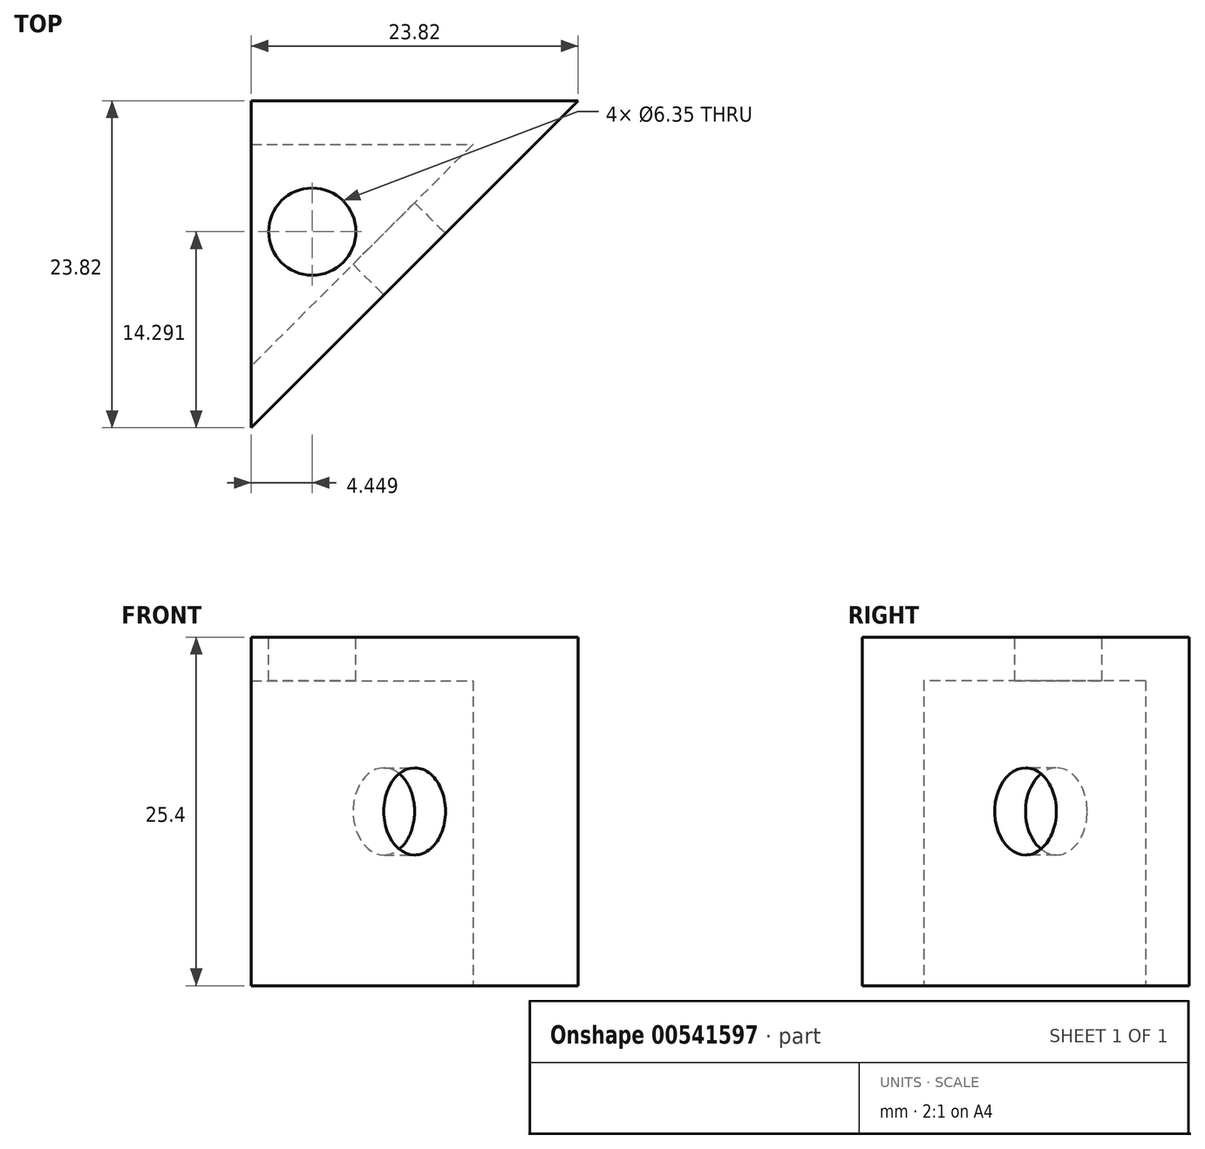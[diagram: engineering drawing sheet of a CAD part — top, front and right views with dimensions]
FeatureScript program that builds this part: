
annotation { "Feature Type Name" : "Feature", "Feature Type Description" : "" }
export const myFeature = defineFeature(function(context is Context, id is Id, definition is map)
    precondition{}
    {
        {
            var Q0;
            Q0=qCreatedBy(makeId("Top.planeOp"),FACE);
            var sketch = newSketch(context, id + "F0", { "sketchPlane" : qUnion([Q0])});
            skLineSegment(sketch, "E0.bottom", {"start": v(-11.9, 11.9) * mm, "end": v(11.9, 11.9) * mm});
            skLineSegment(sketch, "E0.top", {"start": v(-11.9, -11.9) * mm, "end": v(11.9, -11.9) * mm});
            skLineSegment(sketch, "E0.left", {"start": v(-11.9, 11.9) * mm, "end": v(-11.9, -11.9) * mm});
            skLineSegment(sketch, "E0.right", {"start": v(11.9, 11.9) * mm, "end": v(11.9, -11.9) * mm});
            skPoint(sketch, "E0.middle", {"position": v(0, 0) * mm});
            skLineSegment(sketch, "E1", {"start": v(11.9, 11.9) * mm, "end": v(-11.9, -11.9) * mm});
            skSolve(sketch);
        }
        {
            var Q0;
            Q0=makeQuery(id+"F0.imprint","IMPRINT",FACE,{"disambiguationData":[TD([[makeQuery(id+"F0.imprint","IMPRINT",EDGE,{"derivedFrom":sQuery(id+"F0.wireOp",EDGE,"E0.bottom")}),-1.0]])]});
            extrude(context, id + "F1", {"entities" : qUnion([Q0]), "depth" : 25.4 * mm, "offsetDistance" : 25.4 * mm});
        }
        {
            var Q0;
            Q0=makeQuery(id+"F1.opExtrude","SWEPT_FACE",FACE,{"disambiguationData":[OSD([sQuery(id+"F0.wireOp",EDGE,"E0.left")])]});
            shell(context, id + "F2", {"entities" : qUnion([Q0]), "thickness" : 3.17 * mm});
        }
        {
            var Q0;
            {var subQ0=sQuery(id+"F0.wireOp",EDGE,"E1");var subQ1=sQuery(id+"F0.wireOp",EDGE,"E0.left");var subQ2=sQuery(id+"F0.wireOp",EDGE,"E0.bottom");Q0=makeQuery(id+"F2.opShell","OFFSET_FACE",FACE,{"disambiguationData":[OSD([subQ2,subQ1,subQ0]),TDD([makeQuery(id+"F1.opExtrude","CAP_FACE",FACE,{"disambiguationData":[OSD([subQ2,subQ1,subQ0])],"isStart":true})])]});}
            extrude(context, id + "F3", {"entities" : qUnion([Q0]), "operationType" : NewBodyOperationType.REMOVE, "oppositeDirection" : true, "depth" : 25.4 * mm, "offsetDistance" : 25.4 * mm});
        }
        {
            var Q0;
            Q0=makeQuery(id+"F1.opExtrude","SWEPT_FACE",FACE,{"disambiguationData":[OSD([sQuery(id+"F0.wireOp",EDGE,"E0.left")])]});
            var sketch = newSketch(context, id + "F4", { "sketchPlane" : qUnion([Q0])});
            skLineSegment(sketch, "E2", {"start": v(11.9, 25.4) * mm, "end": v(-11.9, 0) * mm});
            skLineSegment(sketch, "E3", {"start": v(-11.9, 25.4) * mm, "end": v(11.9, 0) * mm});
            skCircle(sketch, "E4", {"center": v(0, 12.7) * mm, "radius": 3.18 * mm});
            skSolve(sketch);
        }
        {
            var Q0;
            {var subQ0=sQuery(id+"F4.wireOp",EDGE,"E4");var subQ1=sQuery(id+"F4.wireOp",EDGE,"E2");var subQ2=makeQuery(id+"F4.imprint","INTERSECT",VERTEX,{"disambiguationData":[OD(0.0)],"derivedFrom":[subQ1,subQ0]});Q0=makeQuery(id+"F4.imprint","IMPRINT",FACE,{"disambiguationData":[TD([[makeQuery(id+"F4.imprint","IMPRINT",EDGE,{"disambiguationData":[TD([[subQ2,-1.0]])],"derivedFrom":subQ1}),1.0]])]});}
            var Q1;
            {var subQ0=sQuery(id+"F4.wireOp",EDGE,"E4");var subQ1=sQuery(id+"F4.wireOp",EDGE,"E2");var subQ2=makeQuery(id+"F4.imprint","INTERSECT",VERTEX,{"disambiguationData":[OD(0.0)],"derivedFrom":[subQ1,subQ0]});Q1=makeQuery(id+"F4.imprint","IMPRINT",FACE,{"disambiguationData":[TD([[makeQuery(id+"F4.imprint","IMPRINT",EDGE,{"disambiguationData":[TD([[subQ2,-1.0]])],"derivedFrom":subQ1}),-1.0]])]});}
            var Q2;
            {var subQ0=sQuery(id+"F4.wireOp",EDGE,"E3");var subQ1=sQuery(id+"F4.wireOp",EDGE,"E2");var subQ2=makeQuery(id+"F4.imprint","INTERSECT",VERTEX,{"derivedFrom":[subQ1,subQ0]});Q2=makeQuery(id+"F4.imprint","IMPRINT",FACE,{"disambiguationData":[TD([[makeQuery(id+"F4.imprint","IMPRINT",EDGE,{"disambiguationData":[TD([[subQ2,-1.0]])],"derivedFrom":subQ1}),-1.0]])]});}
            var Q3;
            {var subQ0=sQuery(id+"F4.wireOp",EDGE,"E3");var subQ1=sQuery(id+"F4.wireOp",EDGE,"E2");var subQ2=makeQuery(id+"F4.imprint","INTERSECT",VERTEX,{"derivedFrom":[subQ1,subQ0]});Q3=makeQuery(id+"F4.imprint","IMPRINT",FACE,{"disambiguationData":[TD([[makeQuery(id+"F4.imprint","IMPRINT",EDGE,{"disambiguationData":[TD([[subQ2,-1.0]])],"derivedFrom":subQ1}),1.0]])]});}
            extrude(context, id + "F5", {"entities" : qUnion([Q0, Q1, Q2, Q3]), "operationType" : NewBodyOperationType.REMOVE, "oppositeDirection" : true, "depth" : 3.17 * mm, "offsetDistance" : 25.4 * mm});
        }
        {
            var Q0;
            Q0=makeQuery(id+"F1.opExtrude","CAP_FACE",FACE,{"disambiguationData":[OSD([sQuery(id+"F0.wireOp",EDGE,"E0.bottom"),sQuery(id+"F0.wireOp",EDGE,"E0.left"),sQuery(id+"F0.wireOp",EDGE,"E1")])],"isStart":false});
            var sketch = newSketch(context, id + "F6", { "sketchPlane" : qUnion([Q0])});
            skCircle(sketch, "E5", {"center": v(-7.46, 2.38) * mm, "radius": 3.18 * mm});
            skSolve(sketch);
        }
        {
            var Q0;
            {var subQ0=sQuery(id+"F6.wireOp",EDGE,"E5");var subQ1=sQuery(id+"F6.wireOp",EDGE,"HWwZXyzN-BkNU-UMwY-gXSM-99bSMozpZ1Sp");var subQ2=makeQuery(id+"F6.imprint","INTERSECT",VERTEX,{"disambiguationData":[OD(0.0)],"derivedFrom":[subQ1,subQ0]});Q0=makeQuery(id+"F6.imprint","IMPRINT",FACE,{"disambiguationData":[TD([[makeQuery(id+"F6.imprint","IMPRINT",EDGE,{"disambiguationData":[TD([[subQ2,-1.0]])],"derivedFrom":subQ1}),-1.0]])]});}
            var Q1;
            {var subQ0=sQuery(id+"F6.wireOp",EDGE,"E5");var subQ1=sQuery(id+"F6.wireOp",EDGE,"HWwZXyzN-BkNU-UMwY-gXSM-99bSMozpZ1Sp");var subQ2=makeQuery(id+"F6.imprint","INTERSECT",VERTEX,{"disambiguationData":[OD(0.0)],"derivedFrom":[subQ1,subQ0]});Q1=makeQuery(id+"F6.imprint","IMPRINT",FACE,{"disambiguationData":[TD([[makeQuery(id+"F6.imprint","IMPRINT",EDGE,{"disambiguationData":[TD([[subQ2,-1.0]])],"derivedFrom":subQ1}),1.0]])]});}
            var Q2;
            {var subQ0=sQuery(id+"F6.wireOp",EDGE,"xwTGamvL-BoM2-GFio-XRPn-19hndFO4djhj");var subQ1=sQuery(id+"F6.wireOp",EDGE,"HWwZXyzN-BkNU-UMwY-gXSM-99bSMozpZ1Sp");var subQ2=makeQuery(id+"F6.imprint","INTERSECT",VERTEX,{"derivedFrom":[subQ1,subQ0]});Q2=makeQuery(id+"F6.imprint","IMPRINT",FACE,{"disambiguationData":[TD([[makeQuery(id+"F6.imprint","IMPRINT",EDGE,{"disambiguationData":[TD([[subQ2,-1.0]])],"derivedFrom":subQ1}),-1.0]])]});}
            var Q3;
            {var subQ0=sQuery(id+"F6.wireOp",EDGE,"xwTGamvL-BoM2-GFio-XRPn-19hndFO4djhj");var subQ1=sQuery(id+"F6.wireOp",EDGE,"HWwZXyzN-BkNU-UMwY-gXSM-99bSMozpZ1Sp");var subQ2=makeQuery(id+"F6.imprint","INTERSECT",VERTEX,{"derivedFrom":[subQ1,subQ0]});Q3=makeQuery(id+"F6.imprint","IMPRINT",FACE,{"disambiguationData":[TD([[makeQuery(id+"F6.imprint","IMPRINT",EDGE,{"disambiguationData":[TD([[subQ2,-1.0]])],"derivedFrom":subQ1}),1.0]])]});}
            var Q4;
            Q4=makeQuery(id+"F6.imprint","IMPRINT",FACE,{"disambiguationData":[TD([[makeQuery(id+"F6.imprint","IMPRINT",EDGE,{"derivedFrom":sQuery(id+"F6.wireOp",EDGE,"E5")}),1.0]])]});
            extrude(context, id + "F7", {"entities" : qUnion([Q0, Q1, Q2, Q3, Q4]), "operationType" : NewBodyOperationType.REMOVE, "oppositeDirection" : true, "depth" : 25.4 * mm, "offsetDistance" : 25.4 * mm});
        }
        {
            var Q0;
            Q0=makeQuery(id+"F1.opExtrude","SWEPT_FACE",FACE,{"disambiguationData":[OSD([sQuery(id+"F0.wireOp",EDGE,"E1")])]});
            var sketch = newSketch(context, id + "F8", { "sketchPlane" : qUnion([Q0])});
            skLineSegment(sketch, "E6", {"start": v(-16.84, 25.4) * mm, "end": v(16.84, 0) * mm});
            skCircle(sketch, "E7", {"center": v(0, 12.7) * mm, "radius": 3.18 * mm});
            skSolve(sketch);
        }
        {
            var Q0;
            {var subQ0=sQuery(id+"F8.wireOp",EDGE,"E7");var subQ1=sQuery(id+"F8.wireOp",EDGE,"E6");var subQ2=makeQuery(id+"F8.imprint","INTERSECT",VERTEX,{"disambiguationData":[OD(0.0)],"derivedFrom":[subQ1,subQ0]});Q0=makeQuery(id+"F8.imprint","IMPRINT",FACE,{"disambiguationData":[TD([[makeQuery(id+"F8.imprint","IMPRINT",EDGE,{"disambiguationData":[TD([[subQ2,-1.0]])],"derivedFrom":subQ1}),1.0]])]});}
            var Q1;
            {var subQ0=sQuery(id+"F8.wireOp",EDGE,"E7");var subQ1=sQuery(id+"F8.wireOp",EDGE,"E6");var subQ2=makeQuery(id+"F8.imprint","INTERSECT",VERTEX,{"disambiguationData":[OD(0.0)],"derivedFrom":[subQ1,subQ0]});Q1=makeQuery(id+"F8.imprint","IMPRINT",FACE,{"disambiguationData":[TD([[makeQuery(id+"F8.imprint","IMPRINT",EDGE,{"disambiguationData":[TD([[subQ2,-1.0]])],"derivedFrom":subQ1}),-1.0]])]});}
            extrude(context, id + "F9", {"entities" : qUnion([Q0, Q1]), "operationType" : NewBodyOperationType.REMOVE, "oppositeDirection" : true, "depth" : 3.17 * mm, "offsetDistance" : 25.4 * mm});
        }
    });
